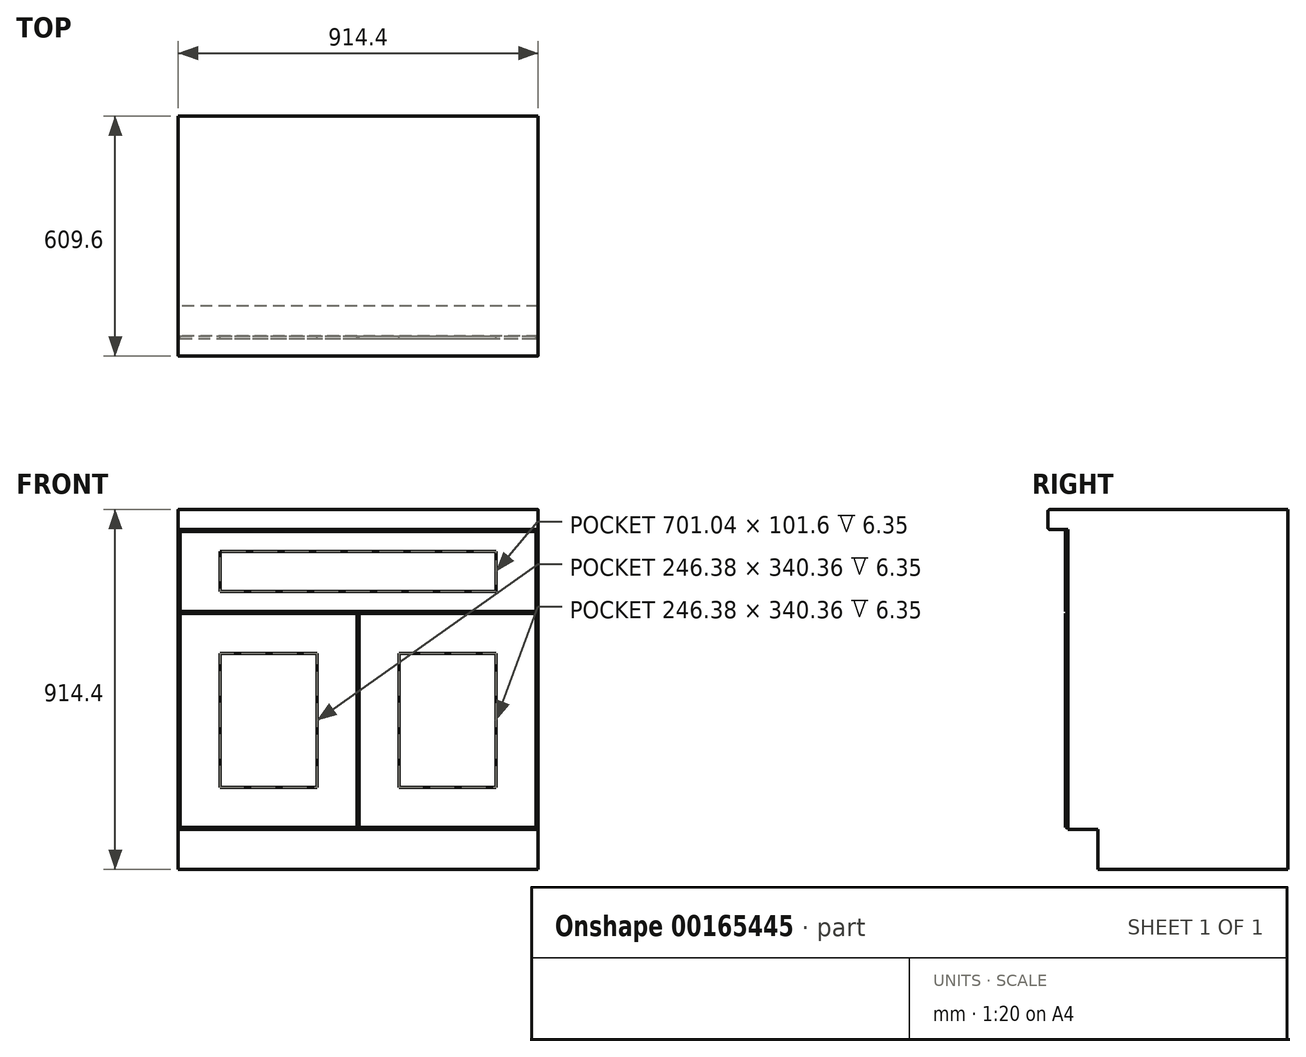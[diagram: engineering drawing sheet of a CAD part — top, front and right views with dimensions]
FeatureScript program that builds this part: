
annotation { "Feature Type Name" : "Feature", "Feature Type Description" : "" }
export const myFeature = defineFeature(function(context is Context, id is Id, definition is map)
    precondition{}
    {
        {
            var Q0;
            Q0=qCreatedBy(makeId("Right.planeOp"),FACE);
            var sketch = newSketch(context, id + "F0", { "sketchPlane" : qUnion([Q0])});
            skLineSegment(sketch, "E0", {"start": v(0, 0) * mm, "end": v(0, 914.4) * mm});
            skLineSegment(sketch, "E1", {"start": v(0, 914.4) * mm, "end": v(-609.6, 914.4) * mm});
            skLineSegment(sketch, "E2", {"start": v(-609.6, 914.4) * mm, "end": v(-609.6, 863.6) * mm});
            skLineSegment(sketch, "E3", {"start": v(-609.6, 863.6) * mm, "end": v(-558.8, 863.6) * mm});
            skLineSegment(sketch, "E4", {"start": v(-558.8, 863.6) * mm, "end": v(-558.8, 101.6) * mm});
            skLineSegment(sketch, "E5", {"start": v(-558.8, 101.6) * mm, "end": v(-482.6, 101.6) * mm});
            skLineSegment(sketch, "E6", {"start": v(-482.6, 101.6) * mm, "end": v(-482.6, 0) * mm});
            skLineSegment(sketch, "E7", {"start": v(-482.6, 0) * mm, "end": v(0, 0) * mm});
            skSolve(sketch);
        }
        {
            var Q0;
            Q0=makeQuery(id+"F0.imprint","IMPRINT",FACE,{"disambiguationData":[TD([[makeQuery(id+"F0.imprint","IMPRINT",EDGE,{"derivedFrom":sQuery(id+"F0.wireOp",EDGE,"E0")}),1.0]])]});
            extrude(context, id + "F1", {"entities" : qUnion([Q0]), "depth" : 914.4 * mm});
        }
        {
            var Q0;
            Q0=makeQuery(id+"F1.opExtrude","SWEPT_EDGE",EDGE,{"disambiguationData":[OSD([sQuery(id+"F0.wireOp",EDGE,"E1"),sQuery(id+"F0.wireOp",EDGE,"E2")])]});
            var Q1;
            Q1=makeQuery(id+"F1.opExtrude","SWEPT_EDGE",EDGE,{"disambiguationData":[OSD([sQuery(id+"F0.wireOp",EDGE,"E2"),sQuery(id+"F0.wireOp",EDGE,"E3")])]});
            fillet(context, id + "F2", {"entities" : qUnion([Q0, Q1]), "radius" : 5.08 * mm, "tangentPropagation" : true, "allowEdgeOverflow" : false});
        }
        {
            var Q0;
            Q0=makeQuery(id+"F1.opExtrude","SWEPT_FACE",FACE,{"disambiguationData":[OSD([sQuery(id+"F0.wireOp",EDGE,"E4")])]});
            var sketch = newSketch(context, id + "F3", { "sketchPlane" : qUnion([Q0])});
            skLineSegment(sketch, "E8.bottom", {"start": v(5.08, 858.52) * mm, "end": v(909.32, 858.52) * mm});
            skLineSegment(sketch, "E8.top", {"start": v(5.08, 655.32) * mm, "end": v(909.32, 655.32) * mm});
            skLineSegment(sketch, "E8.left", {"start": v(5.08, 858.52) * mm, "end": v(5.08, 655.32) * mm});
            skLineSegment(sketch, "E8.right", {"start": v(909.32, 858.52) * mm, "end": v(909.32, 655.32) * mm});
            skLineSegment(sketch, "E9.bottom", {"start": v(5.08, 650.24) * mm, "end": v(454.66, 650.24) * mm});
            skLineSegment(sketch, "E9.top", {"start": v(5.08, 106.68) * mm, "end": v(454.66, 106.68) * mm});
            skLineSegment(sketch, "E9.left", {"start": v(5.08, 650.24) * mm, "end": v(5.08, 106.68) * mm});
            skLineSegment(sketch, "E9.right", {"start": v(454.66, 650.24) * mm, "end": v(454.66, 106.68) * mm});
            skLineSegment(sketch, "E10.bottom", {"start": v(459.74, 650.24) * mm, "end": v(909.32, 650.24) * mm});
            skLineSegment(sketch, "E10.top", {"start": v(459.74, 106.68) * mm, "end": v(909.32, 106.68) * mm});
            skLineSegment(sketch, "E10.left", {"start": v(459.74, 650.24) * mm, "end": v(459.74, 106.68) * mm});
            skLineSegment(sketch, "E10.right", {"start": v(909.32, 650.24) * mm, "end": v(909.32, 106.68) * mm});
            skLineSegment(sketch, "E11.bottom", {"start": v(561.34, 548.64) * mm, "end": v(807.72, 548.64) * mm});
            skLineSegment(sketch, "E11.top", {"start": v(561.34, 208.28) * mm, "end": v(807.72, 208.28) * mm});
            skLineSegment(sketch, "E11.left", {"start": v(561.34, 548.64) * mm, "end": v(561.34, 208.28) * mm});
            skLineSegment(sketch, "E11.right", {"start": v(807.72, 548.64) * mm, "end": v(807.72, 208.28) * mm});
            skLineSegment(sketch, "E12.bottom", {"start": v(106.68, 548.64) * mm, "end": v(353.06, 548.64) * mm});
            skLineSegment(sketch, "E12.top", {"start": v(106.68, 208.28) * mm, "end": v(353.06, 208.28) * mm});
            skLineSegment(sketch, "E12.left", {"start": v(106.68, 548.64) * mm, "end": v(106.68, 208.28) * mm});
            skLineSegment(sketch, "E12.right", {"start": v(353.06, 548.64) * mm, "end": v(353.06, 208.28) * mm});
            skLineSegment(sketch, "E13.bottom", {"start": v(106.68, 807.72) * mm, "end": v(807.72, 807.72) * mm});
            skLineSegment(sketch, "E13.top", {"start": v(106.68, 706.12) * mm, "end": v(807.72, 706.12) * mm});
            skLineSegment(sketch, "E13.right", {"start": v(807.72, 807.72) * mm, "end": v(807.72, 706.12) * mm});
            skLineSegment(sketch, "E14", {"start": v(106.68, 807.72) * mm, "end": v(106.68, 706.12) * mm});
            skSolve(sketch);
        }
        {
            var Q0;
            Q0=makeQuery(id+"F3.imprint","IMPRINT",FACE,{"disambiguationData":[TD([[makeQuery(id+"F3.imprint","IMPRINT",EDGE,{"derivedFrom":sQuery(id+"F3.wireOp",EDGE,"E8.bottom")}),-1.0]])]});
            var Q1;
            Q1=makeQuery(id+"F3.imprint","IMPRINT",FACE,{"disambiguationData":[TD([[makeQuery(id+"F3.imprint","IMPRINT",EDGE,{"derivedFrom":sQuery(id+"F3.wireOp",EDGE,"E8.bottom")}),-1.0]])]});
            var Q2;
            Q2=makeQuery(id+"F3.imprint","IMPRINT",FACE,{"disambiguationData":[TD([[makeQuery(id+"F3.imprint","IMPRINT",EDGE,{"derivedFrom":sQuery(id+"F3.wireOp",EDGE,"E10.bottom")}),-1.0]])]});
            var Q3;
            Q3=makeQuery(id+"F3.imprint","IMPRINT",FACE,{"disambiguationData":[TD([[makeQuery(id+"F3.imprint","IMPRINT",EDGE,{"derivedFrom":sQuery(id+"F3.wireOp",EDGE,"E9.bottom")}),-1.0]])]});
            extrude(context, id + "F4", {"entities" : qUnion([Q0, Q1, Q2, Q3]), "operationType" : NewBodyOperationType.ADD, "depth" : 6.35 * mm});
        }
    });
